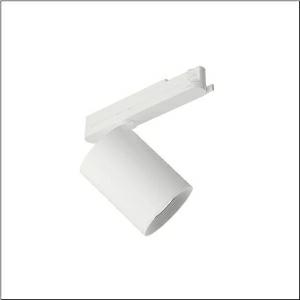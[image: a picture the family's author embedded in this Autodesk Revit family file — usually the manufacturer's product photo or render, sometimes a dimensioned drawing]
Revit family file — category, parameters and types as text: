
# Revit family: spot_21_51se13dba5b
name_source: partatom
category: Lighting Fixtures
units: mm (PartAtom-declared; Revit-internal decimal feet)

## family parameters
Cut with Voids When Loaded = No
Host = Face
Light Source = No
Part Type = Normal
Room Calculation Point = No
Round Connector Dimension = Use Diameter
Shared = No

## types (1)
- --- (1 x LED, 5190 lm, 42.4 W, 2700K)
    Apparent Load = 42 VA
    CIE Flux Codes = 95 98 99 100 100
    Color Rendering = 90
    Color Temperature = 2700K
    Default Elevation = 1800 mm
    Description = Spot 21, directional spotlight, light control with lens, of PMMA, LED rated luminous flux: 4.960lm, light colour: 927, control gear: ECG Multilumen, with 3-phase adapter, mains connection: 220..240V, AC, 50/60Hz, of aluminium, traffic white (RAL 9016), length: 253mm, diameter: 105mm, protection rating (complete): IP20, insulation class (complete): insulation class I (protective earthing), certification: CE, impact resistance: IK02, permissible ambient temperature for indoor applications: -20..+40°C, packaging unit: 1 piece
    Height = 175 mm
    Lamp = 1 x LED
    Lamp Light Flux = 5190 lm
    Lamp Power = 42.4 W
    Lamp count = 1
    Length = 105 mm
    Luminous efficacy = 122 lm/W
    Manufacturer = Siteco
    ModVariant = No
    Model = 51SE13DBA5B
    Mounting Place = Ceiling
    Mounting Type = Pendant
    Number of Poles = 1
    OnlyDefault = Yes
    Power Factor = 1
    Product Name = Spot 21
    Product group = directional spotlight
    ProductGroupID = 906
    Protection Class = Protection class I
    Protection Degree = IP 20
    RLX_Detail_Level = 1
    RLX_Emergency_Light_Flux = 0 lm
    RLX_Emergency_Type = 0
    RLX_Emergency_Type_DB = No
    RlxData = <blob elided: 17585 chars, md5=103cc390>
    Socket = socket
    Standby Power = 0 W
    System Light Flux = 5190 lm
    System Power = 42 W
    Type Comments = factory setting: luminous flux: 100 % | (ON | ON | ON | ON) | 1050 mA
    Type Image = l_1003976.jpg
    URL = http://relux.com
    VarID = @adj_143738
    Voltage = 0 V
    Weight = 0.00 kg
    Width = 0 mm  [stored 0 ft]

note: [stored X ft] marks values corroborated as IEEE doubles in the binary element streams (Revit-internal decimal feet)

## geometry (parser evidence)
native form markers: Blend x4, Sweep x8
no freeform markers — native parametric forms only
